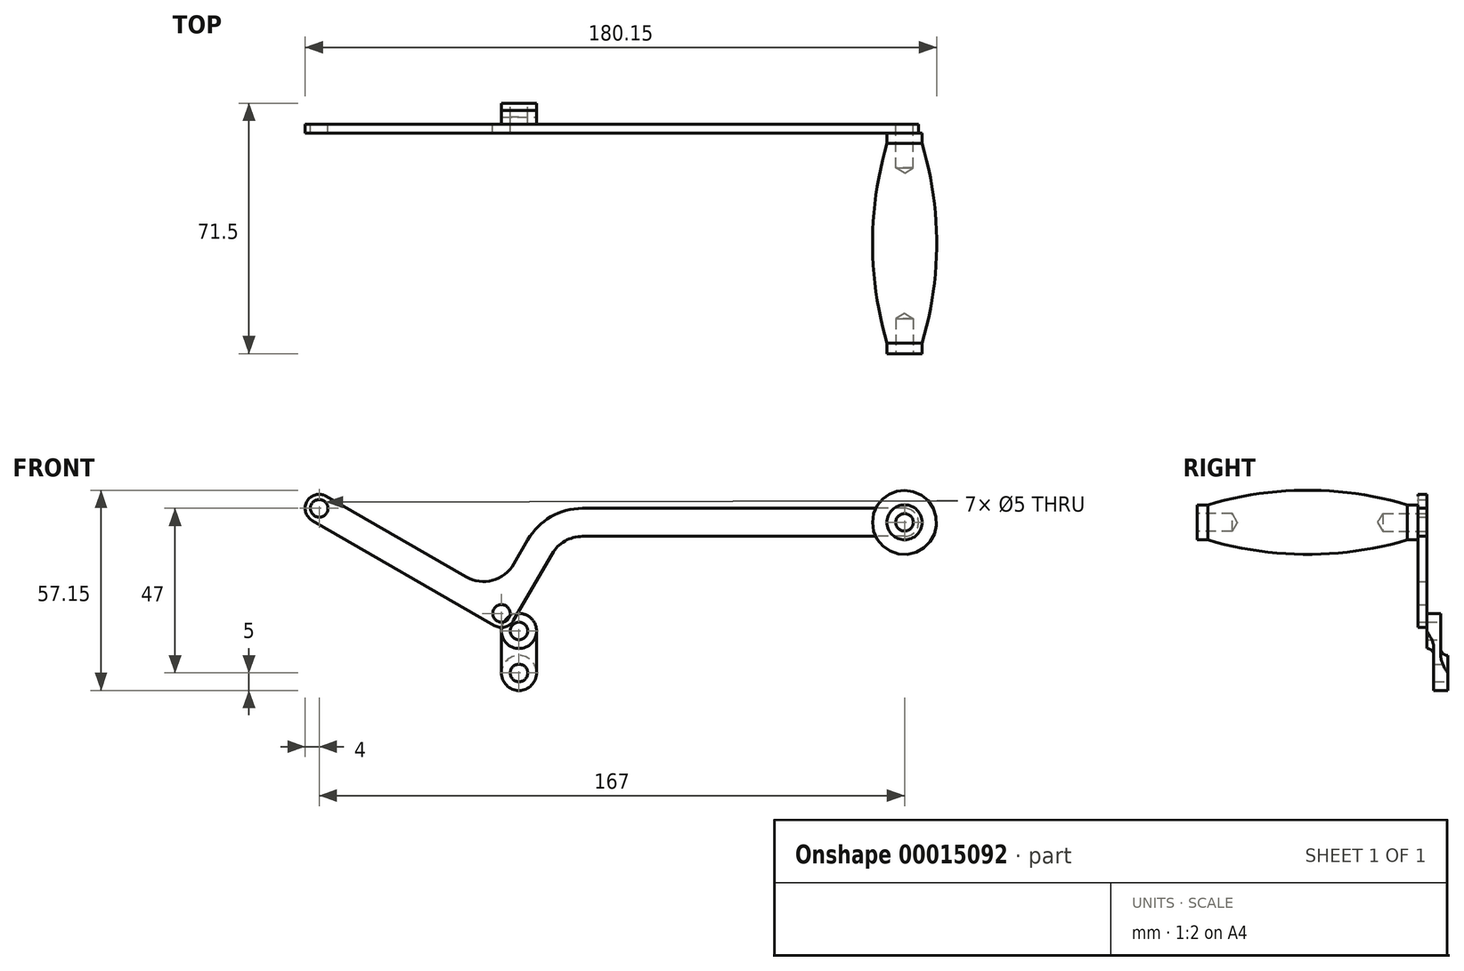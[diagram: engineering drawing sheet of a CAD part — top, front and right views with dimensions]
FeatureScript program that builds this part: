
annotation { "Feature Type Name" : "Feature", "Feature Type Description" : "" }
export const myFeature = defineFeature(function(context is Context, id is Id, definition is map)
    precondition{}
    {
        {
            var Q0;
            Q0=qCreatedBy(makeId("Front.planeOp"),FACE);
            var sketch = newSketch(context, id + "F0", { "sketchPlane" : qUnion([Q0])});
            skCircle(sketch, "E0", {"center": v(0, 0) * mm, "radius": 2.5 * mm});
            skCircle(sketch, "E1", {"center": v(115, 26) * mm, "radius": 2.5 * mm});
            skCircle(sketch, "E2", {"center": v(-52, 30) * mm, "radius": 2.5 * mm});
            skArc(sketch, "E3", {"start": v(-50, 33.46) * mm, "mid": v(-55.46, 32) * mm, "end": v(-54, 26.54) * mm});
            skArc(sketch, "E4", {"start": v(115, 22) * mm, "mid": v(119, 26) * mm, "end": v(115, 30) * mm});
            skLineSegment(sketch, "E5", {"start": v(115, 26) * mm, "end": v(-21.92, 26) * mm, "construction": true});
            skLineSegment(sketch, "E6", {"start": v(-52, 30) * mm, "end": v(-13.37, 30) * mm, "construction": true});
            skLineSegment(sketch, "E7", {"start": v(115, 30) * mm, "end": v(23.1, 30) * mm});
            skLineSegment(sketch, "E8", {"start": v(115, 22) * mm, "end": v(23.1, 22) * mm});
            skLineSegment(sketch, "E9", {"start": v(3.53, 14.12) * mm, "end": v(7.5, 21) * mm});
            skLineSegment(sketch, "E10", {"start": v(3.46, -2) * mm, "end": v(14.43, 17) * mm});
            skLineSegment(sketch, "E11", {"start": v(-50, 33.46) * mm, "end": v(-10.12, 10.46) * mm});
            skLineSegment(sketch, "E12", {"start": v(-2, -3.46) * mm, "end": v(-54, 26.54) * mm});
            skArc(sketch, "E13.filletArc", {"start": v(-10.12, 10.46) * mm, "mid": v(-2.54, 9.46) * mm, "end": v(3.53, 14.12) * mm});
            skArc(sketch, "E14.filletArc", {"start": v(23.1, 22) * mm, "mid": v(18.1, 20.66) * mm, "end": v(14.43, 17) * mm});
            skArc(sketch, "E15.filletArc", {"start": v(23.1, 30) * mm, "mid": v(14.1, 27.59) * mm, "end": v(7.5, 21) * mm});
            skArc(sketch, "E16.filletArc", {"start": v(-2, -3.46) * mm, "mid": v(1.04, -3.86) * mm, "end": v(3.46, -2) * mm});
            skSolve(sketch);
        }
        {
            var Q0;
            Q0=makeQuery(id+"F0.imprint","IMPRINT",FACE,{"disambiguationData":[TD([[makeQuery(id+"F0.imprint","IMPRINT",EDGE,{"derivedFrom":sQuery(id+"F0.wireOp",EDGE,"E0")}),-1.0]])]});
            extrude(context, id + "F1", {"entities" : qUnion([Q0]), "depth" : 2.5 * mm});
        }
        {
            var Q0;
            Q0=makeQuery(id+"F1.opExtrude","CAP_FACE",FACE,{"disambiguationData":[OSD([sQuery(id+"F0.wireOp",EDGE,"E0"),sQuery(id+"F0.wireOp",EDGE,"E1"),sQuery(id+"F0.wireOp",EDGE,"E2"),sQuery(id+"F0.wireOp",EDGE,"E3"),sQuery(id+"F0.wireOp",EDGE,"E4"),sQuery(id+"F0.wireOp",EDGE,"E7"),sQuery(id+"F0.wireOp",EDGE,"E8"),sQuery(id+"F0.wireOp",EDGE,"E9"),sQuery(id+"F0.wireOp",EDGE,"E10"),sQuery(id+"F0.wireOp",EDGE,"E11"),sQuery(id+"F0.wireOp",EDGE,"E12"),sQuery(id+"F0.wireOp",EDGE,"E13.filletArc"),sQuery(id+"F0.wireOp",EDGE,"E14.filletArc"),sQuery(id+"F0.wireOp",EDGE,"E15.filletArc"),sQuery(id+"F0.wireOp",EDGE,"E16.filletArc")])],"isStart":false});
            var sketch = newSketch(context, id + "F2", { "sketchPlane" : qUnion([Q0])});
            skCircle(sketch, "E17.0", {"center": v(115, 26) * mm, "radius": 2.5 * mm});
            skCircle(sketch, "E18", {"center": v(115, 26) * mm, "radius": 5 * mm});
            skSolve(sketch);
        }
        {
            var Q0;
            Q0=makeQuery(id+"F2.imprint","IMPRINT",FACE,{"disambiguationData":[TD([[makeQuery(id+"F2.imprint","IMPRINT",EDGE,{"derivedFrom":sQuery(id+"F2.wireOp",EDGE,"E17.0")}),-1.0]])]});
            var Q1;
            Q1=makeQuery(id+"F2.imprint","IMPRINT",FACE,{"disambiguationData":[TD([[makeQuery(id+"F2.imprint","IMPRINT",EDGE,{"derivedFrom":sQuery(id+"F2.wireOp",EDGE,"E17.0")}),1.0]])]});
            var Q2;
            {var subQ3=makeQuery(id+"F1.opExtrude","CAP_EDGE",EDGE,{"disambiguationData":[OSD([sQuery(id+"F0.wireOp",EDGE,"E4")])],"isStart":false});Q2=makeQuery(id+"F2.imprint","IMPRINT",FACE,{"disambiguationData":[TD([[makeQuery(id+"F2.imprint","IMPRINT",EDGE,{"derivedFrom":subQ3}),-1.0]])]});}
            extrude(context, id + "F3", {"entities" : qUnion([Q0, Q1, Q2]), "depth" : 63 * mm});
        }
        {
            var Q0;
            Q0=qCreatedBy(makeId("Right.planeOp"),FACE);
            var Q1;
            Q1=sQuery(id+"F2.wireOp",VERTEX,"E17.0.center");
            cPlane(context, id + "F4", {"entities" : qUnion([Q0, Q1]), "cplaneType" : CPlaneType.PLANE_POINT, "offset" : 150 * mm, "width" : 150 * mm, "height" : 150 * mm});
        }
        {
            var Q0;
            Q0=qCreatedBy(id+"F4.planeOp",FACE);
            var sketch = newSketch(context, id + "F5", { "sketchPlane" : qUnion([Q0])});
            skPoint(sketch, "E19.0", {"position": v(-2.5, 26) * mm});
            skLineSegment(sketch, "E20", {"start": v(-2.5, 26) * mm, "end": v(-67.15, 26) * mm});
            skLineSegment(sketch, "E21.0", {"start": v(-65.5, 21) * mm, "end": v(-65.5, 31) * mm});
            skLineSegment(sketch, "E22.0", {"start": v(-2.5, 21) * mm, "end": v(-2.5, 31) * mm});
            skLineSegment(sketch, "E23.0", {"start": v(-62.5, 21) * mm, "end": v(-62.5, 31) * mm});
            skLineSegment(sketch, "E24.0", {"start": v(-5.5, 21) * mm, "end": v(-5.5, 31) * mm});
            skArc(sketch, "E25", {"start": v(-5.5, 31) * mm, "mid": v(-34, 35.15) * mm, "end": v(-62.5, 31) * mm});
            skSolve(sketch);
        }
        {
            var Q0;
            {var subQ0=sQuery(id+"F5.wireOp",EDGE,"E25");Q0=makeQuery(id+"F5.imprint","IMPRINT",FACE,{"disambiguationData":[TD([[makeQuery(id+"F5.imprint","IMPRINT",EDGE,{"derivedFrom":subQ0}),1.0]])]});}
            var Q1;
            Q1=sQuery(id+"F5.wireOp",EDGE,"E20");
            revolve(context, id + "F6", {"operationType" : NewBodyOperationType.ADD, "entities" : qUnion([Q0]), "axis" : qUnion([Q1]), "revolveType" : RevolveType.FULL});
        }
        {
            var Q0;
            Q0=sQuery(id+"F2.wireOp",VERTEX,"E18.center");
            var Q1;
            Q1=makeQuery(id+"F3.opExtrude","SWEPT_BODY",BODY,{"disambiguationData":[OSD([sQuery(id+"F2.wireOp",EDGE,"E18")])]});
            hole(context, id + "F7", {"style" : HoleStyle.SIMPLE, "holeDiameter" : 5 * mm, "endStyle" : HoleEndStyle.BLIND, "oppositeDirection" : true, "holeDepth" : 10 * mm, "locations" : qUnion([Q0]), "scope" : qUnion([Q1])});
        }
        {
            var Q0;
            Q0=makeQuery(id+"F3.opExtrude","CAP_FACE",FACE,{"disambiguationData":[OSD([sQuery(id+"F2.wireOp",EDGE,"E18")])],"isStart":false});
            var sketch = newSketch(context, id + "F8", { "sketchPlane" : qUnion([Q0])});
            skCircle(sketch, "E26.0.0", {"center": v(115, 26) * mm, "radius": 5 * mm});
            skSolve(sketch);
        }
        {
            var Q0;
            Q0=sQuery(id+"F8.wireOp",VERTEX,"E26.0.0.center");
            var Q1;
            Q1=makeQuery(id+"F3.opExtrude","SWEPT_BODY",BODY,{"disambiguationData":[OSD([sQuery(id+"F2.wireOp",EDGE,"E18")])]});
            hole(context, id + "F9", {"style" : HoleStyle.SIMPLE, "holeDiameter" : 5 * mm, "endStyle" : HoleEndStyle.BLIND, "holeDepth" : 10 * mm, "locations" : qUnion([Q0]), "scope" : qUnion([Q1])});
        }
        {
            var Q0;
            Q0=qCreatedBy(makeId("Right.planeOp"),FACE);
            var sketch = newSketch(context, id + "F10", { "sketchPlane" : qUnion([Q0])});
            skLineSegment(sketch, "E27.bottom", {"start": v(0, 0) * mm, "end": v(6, 0) * mm});
            skLineSegment(sketch, "E27.top", {"start": v(0, -22) * mm, "end": v(6, -22) * mm});
            skLineSegment(sketch, "E27.left", {"start": v(0, 0) * mm, "end": v(0, -22) * mm});
            skLineSegment(sketch, "E27.right", {"start": v(6, 0) * mm, "end": v(6, -22) * mm});
            skLineSegment(sketch, "E28", {"start": v(4, 0) * mm, "end": v(4, -10) * mm});
            skLineSegment(sketch, "E29", {"start": v(2, -22) * mm, "end": v(2, -12) * mm});
            skLineSegment(sketch, "E30", {"start": v(0, -5) * mm, "end": v(6, -5) * mm, "construction": true});
            skLineSegment(sketch, "E31", {"start": v(0, -17) * mm, "end": v(6, -17) * mm, "construction": true});
            skLineSegment(sketch, "E32.0", {"start": v(0, -7.5) * mm, "end": v(6, -7.5) * mm, "construction": true});
            skLineSegment(sketch, "E33.0", {"start": v(0, -2.5) * mm, "end": v(6, -2.5) * mm, "construction": true});
            skLineSegment(sketch, "E34.0", {"start": v(0, -19.5) * mm, "end": v(6, -19.5) * mm, "construction": true});
            skLineSegment(sketch, "E35.0", {"start": v(0, -14.5) * mm, "end": v(6, -14.5) * mm, "construction": true});
            skLineSegment(sketch, "E36", {"start": v(0, -10) * mm, "end": v(6, -10) * mm, "construction": true});
            skLineSegment(sketch, "E37", {"start": v(0, -12) * mm, "end": v(6, -12) * mm, "construction": true});
            skArc(sketch, "E38", {"start": v(4, -10) * mm, "mid": v(4.59, -11.41) * mm, "end": v(6, -12) * mm});
            skArc(sketch, "E39", {"start": v(2, -12) * mm, "mid": v(1.41, -10.59) * mm, "end": v(0, -10) * mm});
            skSolve(sketch);
        }
        {
            var Q0;
            {var subQ3=sQuery(id+"F10.wireOp",EDGE,"E28");Q0=makeQuery(id+"F10.imprint","IMPRINT",FACE,{"disambiguationData":[TD([[makeQuery(id+"F10.imprint","IMPRINT",EDGE,{"derivedFrom":subQ3}),-1.0]])]});}
            extrude(context, id + "F11", {"entities" : qUnion([Q0]), "depth" : 10 * mm});
        }
        {
            var Q0;
            Q0=makeQuery(id+"F11.opExtrude","CAP_EDGE",EDGE,{"disambiguationData":[OSD([sQuery(id+"F10.wireOp",EDGE,"E27.bottom")])],"isStart":false});
            var Q1;
            Q1=makeQuery(id+"F11.opExtrude","CAP_EDGE",EDGE,{"disambiguationData":[OSD([sQuery(id+"F10.wireOp",EDGE,"E27.bottom")])],"isStart":true});
            var Q2;
            Q2=makeQuery(id+"F11.opExtrude","CAP_EDGE",EDGE,{"disambiguationData":[OSD([sQuery(id+"F10.wireOp",EDGE,"E27.top")])],"isStart":false});
            var Q3;
            Q3=makeQuery(id+"F11.opExtrude","CAP_EDGE",EDGE,{"disambiguationData":[OSD([sQuery(id+"F10.wireOp",EDGE,"E27.top")])],"isStart":true});
            fillet(context, id + "F12", {"entities" : qUnion([Q0, Q1, Q2, Q3]), "radius" : 5 * mm, "tangentPropagation" : true, "allowEdgeOverflow" : false});
        }
        {
            var Q0;
            Q0=makeQuery(id+"F11.opExtrude","SWEPT_FACE",FACE,{"disambiguationData":[OSD([sQuery(id+"F10.wireOp",EDGE,"E27.right")])]});
            var sketch = newSketch(context, id + "F13", { "sketchPlane" : qUnion([Q0])});
            skArc(sketch, "E40.0", {"start": v(-10, -17) * mm, "mid": v(-5, -22) * mm, "end": v(0, -17) * mm});
            skArc(sketch, "E41.0", {"start": v(0, -5) * mm, "mid": v(-5, 0) * mm, "end": v(-10, -5) * mm});
            skCircle(sketch, "E42", {"center": v(-5, -5) * mm, "radius": 5 * mm});
            skLineSegment(sketch, "E43.0.0", {"start": v(0, -12) * mm, "end": v(0, -17) * mm});
            skArc(sketch, "E43.0.1", {"start": v(0, -17) * mm, "mid": v(-5, -22) * mm, "end": v(-10, -17) * mm});
            skLineSegment(sketch, "E43.0.2", {"start": v(-10, -17) * mm, "end": v(-10, -12) * mm});
            skLineSegment(sketch, "E43.0.3", {"start": v(-10, -12) * mm, "end": v(0, -12) * mm});
            skLineSegment(sketch, "E44.0.0", {"start": v(0, -10) * mm, "end": v(0, -12) * mm});
            skLineSegment(sketch, "E44.0.1", {"start": v(0, -12) * mm, "end": v(-10, -12) * mm});
            skLineSegment(sketch, "E44.0.2", {"start": v(-10, -12) * mm, "end": v(-10, -10) * mm});
            skLineSegment(sketch, "E44.0.3", {"start": v(-10, -10) * mm, "end": v(0, -10) * mm});
            skArc(sketch, "E45.0.0", {"start": v(-10, -5) * mm, "mid": v(-5, 0) * mm, "end": v(0, -5) * mm});
            skLineSegment(sketch, "E45.0.1", {"start": v(0, -5) * mm, "end": v(0, -10) * mm});
            skLineSegment(sketch, "E45.0.2", {"start": v(0, -10) * mm, "end": v(-10, -10) * mm});
            skLineSegment(sketch, "E45.0.3", {"start": v(-10, -10) * mm, "end": v(-10, -5) * mm});
            skCircle(sketch, "E46", {"center": v(-5, -17) * mm, "radius": 5 * mm});
            skSolve(sketch);
        }
        {
            var Q0;
            {var subQ5=sQuery(id+"F13.wireOp",EDGE,"E44.0.0");Q0=makeQuery(id+"F13.imprint","IMPRINT",FACE,{"disambiguationData":[TD([[makeQuery(id+"F13.imprint","IMPRINT",EDGE,{"derivedFrom":subQ5}),-1.0]])]});}
            var Q1;
            {var subQ3=sQuery(id+"F13.wireOp",EDGE,"E43.0.2");Q1=makeQuery(id+"F13.imprint","IMPRINT",FACE,{"disambiguationData":[TD([[makeQuery(id+"F13.imprint","IMPRINT",EDGE,{"derivedFrom":subQ3}),1.0]])]});}
            var Q2;
            {var subQ3=sQuery(id+"F13.wireOp",EDGE,"E43.0.0");Q2=makeQuery(id+"F13.imprint","IMPRINT",FACE,{"disambiguationData":[TD([[makeQuery(id+"F13.imprint","IMPRINT",EDGE,{"derivedFrom":subQ3}),-1.0]])]});}
            var Q3;
            Q3=makeQuery(id+"F11.opExtrude","SWEPT_FACE",FACE,{"disambiguationData":[OSD([sQuery(id+"F10.wireOp",EDGE,"E38")])]});
            extrude(context, id + "F14", {"entities" : qUnion([Q0, Q1, Q2]), "operationType" : NewBodyOperationType.REMOVE, "oppositeDirection" : true, "endBoundEntity" : qUnion([Q3]), "depth" : 2 * mm});
        }
        {
            var Q0;
            Q0=makeQuery(id+"F11.opExtrude","SWEPT_FACE",FACE,{"disambiguationData":[OSD([sQuery(id+"F10.wireOp",EDGE,"E27.left")])]});
            var sketch = newSketch(context, id + "F15", { "sketchPlane" : qUnion([Q0])});
            skArc(sketch, "E47.0", {"start": v(10, -5) * mm, "mid": v(5, 0) * mm, "end": v(0, -5) * mm});
            skCircle(sketch, "E48", {"center": v(5, -5) * mm, "radius": 5 * mm});
            skLineSegment(sketch, "E49.0.0", {"start": v(0, -12) * mm, "end": v(0, -10) * mm});
            skLineSegment(sketch, "E49.0.1", {"start": v(0, -12) * mm, "end": v(10, -12) * mm});
            skLineSegment(sketch, "E49.0.2", {"start": v(10, -10) * mm, "end": v(10, -12) * mm});
            skLineSegment(sketch, "E49.0.3", {"start": v(10, -10) * mm, "end": v(0, -10) * mm});
            skLineSegment(sketch, "E50.0.0", {"start": v(0, -12) * mm, "end": v(0, -17) * mm});
            skArc(sketch, "E50.0.1", {"start": v(0, -17) * mm, "mid": v(5, -22) * mm, "end": v(10, -17) * mm});
            skLineSegment(sketch, "E50.0.2", {"start": v(10, -17) * mm, "end": v(10, -12) * mm});
            skLineSegment(sketch, "E50.0.3", {"start": v(10, -12) * mm, "end": v(0, -12) * mm});
            skSolve(sketch);
        }
        {
            var Q0;
            {var subQ0=makeQuery(id+"F11.opExtrude","CAP_EDGE",EDGE,{"disambiguationData":[OSD([sQuery(id+"F10.wireOp",EDGE,"E27.left")])],"isStart":false});Q0=makeQuery(id+"F15.imprint","IMPRINT",FACE,{"disambiguationData":[TD([[makeQuery(id+"F15.imprint","IMPRINT",EDGE,{"derivedFrom":subQ0}),-1.0]])]});}
            var Q1;
            {var subQ0=makeQuery(id+"F11.opExtrude","CAP_EDGE",EDGE,{"disambiguationData":[OSD([sQuery(id+"F10.wireOp",EDGE,"E27.left")])],"isStart":true});Q1=makeQuery(id+"F15.imprint","IMPRINT",FACE,{"disambiguationData":[TD([[makeQuery(id+"F15.imprint","IMPRINT",EDGE,{"derivedFrom":subQ0}),1.0]])]});}
            var Q2;
            {var subQ3=sQuery(id+"F15.wireOp",EDGE,"E49.0.0");Q2=makeQuery(id+"F15.imprint","IMPRINT",FACE,{"disambiguationData":[TD([[makeQuery(id+"F15.imprint","IMPRINT",EDGE,{"derivedFrom":subQ3}),-1.0]])]});}
            extrude(context, id + "F16", {"entities" : qUnion([Q0, Q1, Q2]), "operationType" : NewBodyOperationType.REMOVE, "oppositeDirection" : true, "depth" : 2 * mm});
        }
        {
            var Q0;
            Q0=makeQuery(id+"F16.boolean.opBoolean","COPY",EDGE,{"derivedFrom":makeQuery(id+"F16.opExtrude","CAP_EDGE",EDGE,{"disambiguationData":[OSD([sQuery(id+"F15.wireOp",EDGE,"E48")])],"isStart":false})});
            var Q1;
            Q1=makeQuery(id+"F14.boolean.opBoolean","COPY",EDGE,{"derivedFrom":makeQuery(id+"F14.opExtrude","CAP_EDGE",EDGE,{"disambiguationData":[OSD([sQuery(id+"F13.wireOp",EDGE,"E46")])],"isStart":false})});
            fillet(context, id + "F17", {"entities" : qUnion([Q0, Q1]), "radius" : 2 * mm, "tangentPropagation" : true, "allowEdgeOverflow" : false});
        }
        {
            var Q0;
            Q0=sQuery(id+"F13.wireOp",VERTEX,"E41.0.center");
            var Q1;
            Q1=sQuery(id+"F13.wireOp",VERTEX,"E40.0.center");
            var Q2;
            Q2=makeQuery(id+"F11.opExtrude","SWEPT_BODY",BODY,{"disambiguationData":[OSD([sQuery(id+"F10.wireOp",EDGE,"E27.bottom"),sQuery(id+"F10.wireOp",EDGE,"E27.top"),sQuery(id+"F10.wireOp",EDGE,"E27.left"),sQuery(id+"F10.wireOp",EDGE,"E27.right"),sQuery(id+"F10.wireOp",EDGE,"E28"),sQuery(id+"F10.wireOp",EDGE,"E29"),sQuery(id+"F10.wireOp",EDGE,"E38"),sQuery(id+"F10.wireOp",EDGE,"E39")])]});
            hole(context, id + "F18", {"style" : HoleStyle.SIMPLE, "holeDiameter" : 5 * mm, "endStyle" : HoleEndStyle.THROUGH, "locations" : qUnion([Q0, Q1]), "scope" : qUnion([Q2])});
        }
    });
